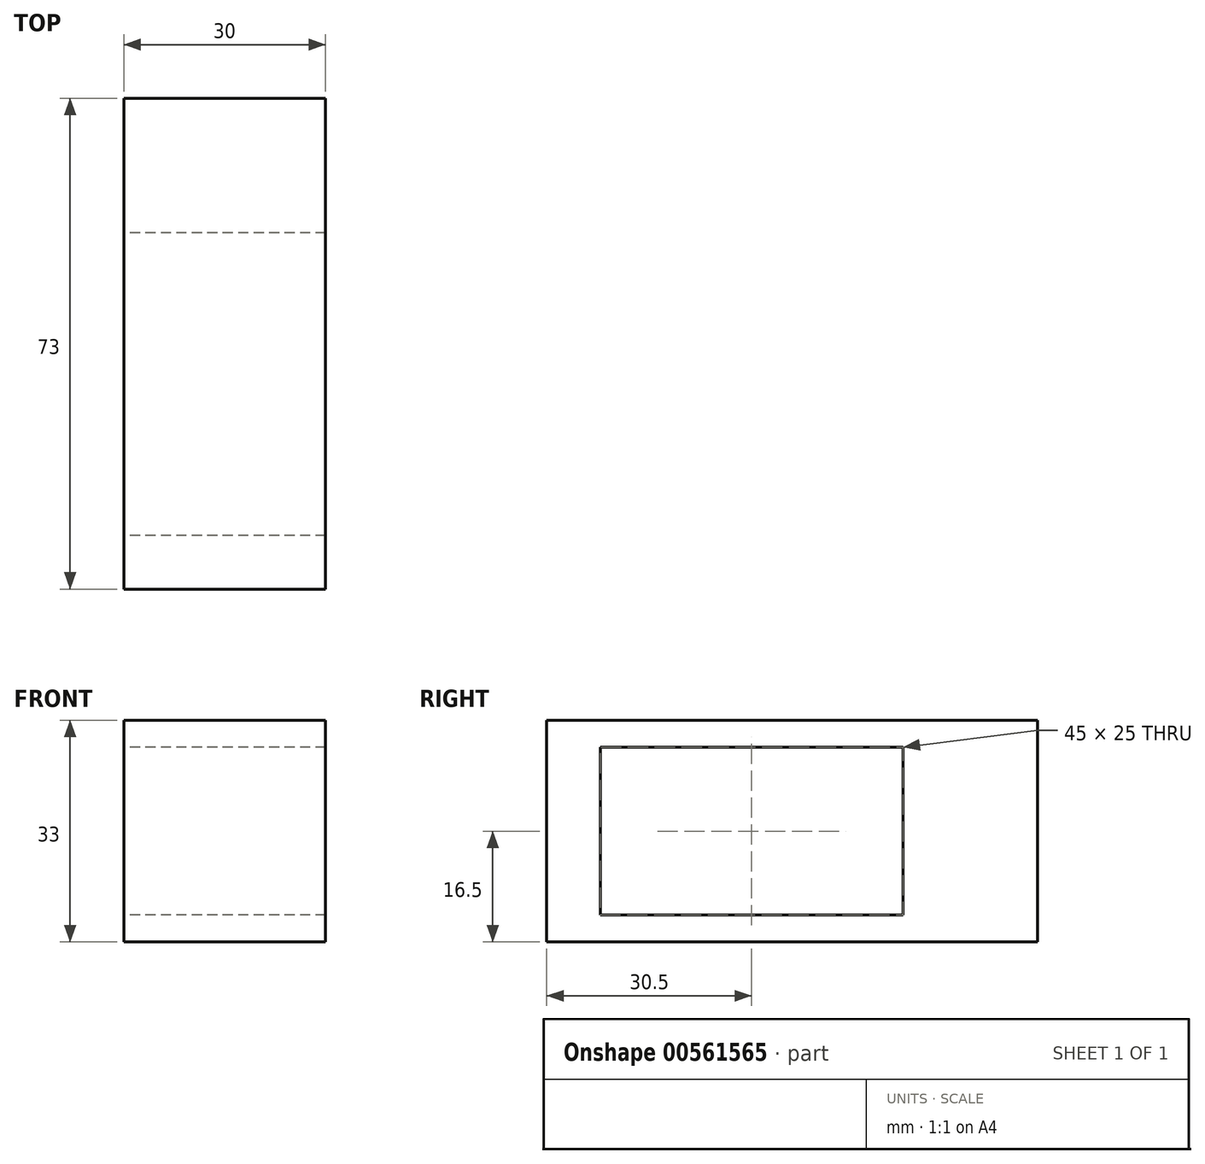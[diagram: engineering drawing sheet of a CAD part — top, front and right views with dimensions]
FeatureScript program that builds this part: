
annotation { "Feature Type Name" : "Feature", "Feature Type Description" : "" }
export const myFeature = defineFeature(function(context is Context, id is Id, definition is map)
    precondition{}
    {
        {
            var Q0;
            Q0=qCreatedBy(makeId("Right.planeOp"),FACE);
            var sketch = newSketch(context, id + "F0", { "sketchPlane" : qUnion([Q0])});
            skLineSegment(sketch, "E0.bottom", {"start": v(0, 0) * mm, "end": v(45, 0) * mm});
            skLineSegment(sketch, "E0.top", {"start": v(0, 25) * mm, "end": v(45, 25) * mm});
            skLineSegment(sketch, "E0.left", {"start": v(0, 0) * mm, "end": v(0, 25) * mm});
            skLineSegment(sketch, "E0.right", {"start": v(45, 0) * mm, "end": v(45, 25) * mm});
            skLineSegment(sketch, "E1.bottom", {"start": v(0, 29) * mm, "end": v(-8, 29) * mm});
            skLineSegment(sketch, "E1.top", {"start": v(0, -4) * mm, "end": v(-8, -4) * mm});
            skLineSegment(sketch, "E1.left", {"start": v(0, 29) * mm, "end": v(0, -4) * mm});
            skLineSegment(sketch, "E1.right", {"start": v(-8, 29) * mm, "end": v(-8, -4) * mm});
            skLineSegment(sketch, "E2.bottom", {"start": v(45, 29) * mm, "end": v(65, 29) * mm});
            skLineSegment(sketch, "E2.top", {"start": v(45, -4) * mm, "end": v(65, -4) * mm});
            skLineSegment(sketch, "E2.left", {"start": v(45, 29) * mm, "end": v(45, -4) * mm});
            skLineSegment(sketch, "E2.right", {"start": v(65, 29) * mm, "end": v(65, -4) * mm});
            skLineSegment(sketch, "E3", {"start": v(0, 29) * mm, "end": v(45, 29) * mm});
            skLineSegment(sketch, "E4", {"start": v(0, -4) * mm, "end": v(45, -4) * mm});
            skSolve(sketch);
        }
        {
            var Q0;
            {var subQ3=sQuery(id+"F0.wireOp",EDGE,"E1.bottom");Q0=makeQuery(id+"F0.imprint","IMPRINT",FACE,{"disambiguationData":[TD([[makeQuery(id+"F0.imprint","IMPRINT",EDGE,{"derivedFrom":subQ3}),1.0]])]});}
            var Q1;
            {var subQ0=sQuery(id+"F0.wireOp",EDGE,"E0.top");Q1=makeQuery(id+"F0.imprint","IMPRINT",FACE,{"disambiguationData":[TD([[makeQuery(id+"F0.imprint","IMPRINT",EDGE,{"derivedFrom":subQ0}),1.0]])]});}
            var Q2;
            {var subQ0=sQuery(id+"F0.wireOp",EDGE,"E0.bottom");Q2=makeQuery(id+"F0.imprint","IMPRINT",FACE,{"disambiguationData":[TD([[makeQuery(id+"F0.imprint","IMPRINT",EDGE,{"derivedFrom":subQ0}),-1.0]])]});}
            var Q3;
            {var subQ3=sQuery(id+"F0.wireOp",EDGE,"E2.bottom");Q3=makeQuery(id+"F0.imprint","IMPRINT",FACE,{"disambiguationData":[TD([[makeQuery(id+"F0.imprint","IMPRINT",EDGE,{"derivedFrom":subQ3}),-1.0]])]});}
            extrude(context, id + "F1", {"entities" : qUnion([Q0, Q1, Q2, Q3]), "depth" : 30 * mm});
        }
    });
